# Revit family: FM-CT8X120
name_source: partatom
category: Detail Items
revit_build: Autodesk Revit 2016 (Build: 20150220_1215(x64)
units: mm (PartAtom-declared; Revit-internal decimal feet)

## family parameters
OmniClass Number = 23.20.40.11.24.14
OmniClass Title = Wood Connectors
Rotate with component = No
Shared = No

## types (2) — shared parameters
Density = 0.09 kg
Description = Connector Other
EPD = https://www.strongtie.eu
ETA / DoP = https://www.strongtie.eu
Manufacturer = Simpson Strong-Tie
Model = FM-CT8X120
Model Disclaimer = Contact Simpson Strong-Tie Company  for more information
Model ID = -
Name = FM-CT8X120
ObjectType = FM-CT8X120
Product Material = White zinc plated
Product Type = Connector Other
Reference = 05297B0812040
Technical datasheet = https://www.strongtie.eu
URL = www.strongtie.eu
UniClass Number = Pr_20_29_76_98
UniClass Title = Wood screws
_visibleleft = No
_visibleright = No

## per-type parameters (varying)
| type | _visiblefront | _visibletop |
| SST_FM-CT8X120_Front | Yes | No |
| SST_FM-CT8X120_Top | No | Yes |

## geometry (parser evidence)
native form markers: Sweep x2
no freeform markers — native parametric forms only
